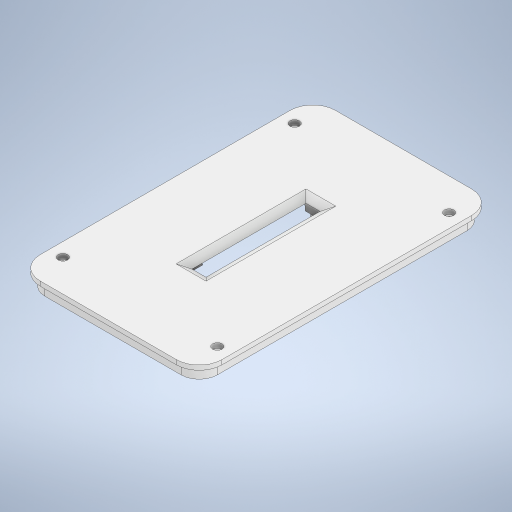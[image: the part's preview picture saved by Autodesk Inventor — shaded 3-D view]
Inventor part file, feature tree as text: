
AUTODESK INVENTOR PART (.ipt)
format: ipt  version: 2023 (Build 270158000, 158)  size: 419,328 bytes
history: native  units: mm
features: extrude x10, sketch x8, plane x2, fillet x2, chamfer x1
ambient origin geometry x8: Origin, YZ Plane, XZ Plane, XY Plane, X Axis, Y Axis, Z Axis, Center Point
bodies: Solid1 (feature_tree)
feature tree (23):
  extrude  "Extrusion1"  Depth=130.0mm
  extrude  "Extrusion2"  Depth=2.0mm
  sketch  "Sketch3"  dims[d4=0.0mm d5=2.1mm]
  extrude  "Extrusion3"  Depth=2.1mm
  extrude  "Extrusion4"  Depth=2.1mm
  extrude  "Extrusion5"  Depth=7.9mm
  plane  "Work Plane1"
  extrude  "Extrusion6"  Depth=4.9mm
  fillet  "Fillet1"  [1 undecoded]
  extrude  "Extrusion7"  Depth=2.0mm
  plane  "Work Plane2"
  sketch  "Sketch8"  dims[d13=2.2mm d14=2.0mm]
  extrude  "Extrusion8"  Depth=3.5mm
  extrude  "Extrusion10"  Depth=3.5mm
  extrude  "Extrusion9"  Depth=102.0mm
  fillet  "Fillet2"  Radius=4.9mm
  chamfer  "Chamfer1"  [1 undecoded]
  sketch  "Sketch1"  dims[d0=80.0mm d1=130.0mm]
  sketch  "Sketch2"  dims[d2=10.0mm d3=2.0mm]
  sketch  "Sketch4"  dims[d6=2.1mm d7=2.1mm]
  sketch  "Sketch6"  dims[d8=2.1mm d9=7.9mm]
  sketch  "Sketch7"  dims[d10=2.0mm d11=4.9mm d12=0.0mm]
  sketch  "Sketch9"  dims[d15=14.0mm d16=6.0mm d17=20.0mm d19=68.0mm d20=20.0mm d22=102.0mm d25=4.9mm d26=0.0mm d27=10.0mm d28=0.0mm d29=4.2mm d30=14.0mm d31=6.0mm d32=20.0mm d34=102.0mm d35=20.0mm d37=68.0mm d40=2.1mm d41=0.0mm d45=-100.0mm d46=22.0mm d47=14.0mm d48=2.0mm d49=2.2mm d50=2.2mm d54=15.4mm d55=10.0mm d56=2.0mm d57=0.0mm d58=2.0mm d59=10.0mm d60=60.0deg d61=50.2mm d62=6.2mm d63=39.5mm d64=2.0mm d65=2.0mm d67=5.7mm d68=0.0mm d69=38.2mm d70=51.1mm d71=45.0deg d72=45.0deg d73=5.7mm d74=24.8mm d75=2.0mm d76=2.0mm d77=12.0mm d78=0.0mm d79=2.0mm d80=2.0mm d81=2.0mm d82=45.0deg d83=51.0mm d84=2.0mm d85=3.5mm d86=0.0mm]
note: 2 required parameter values undecoded (feature->parameter linkage not recoverable at this tier; creation-order binding heuristic only, values carry confidence <= 0.55)
